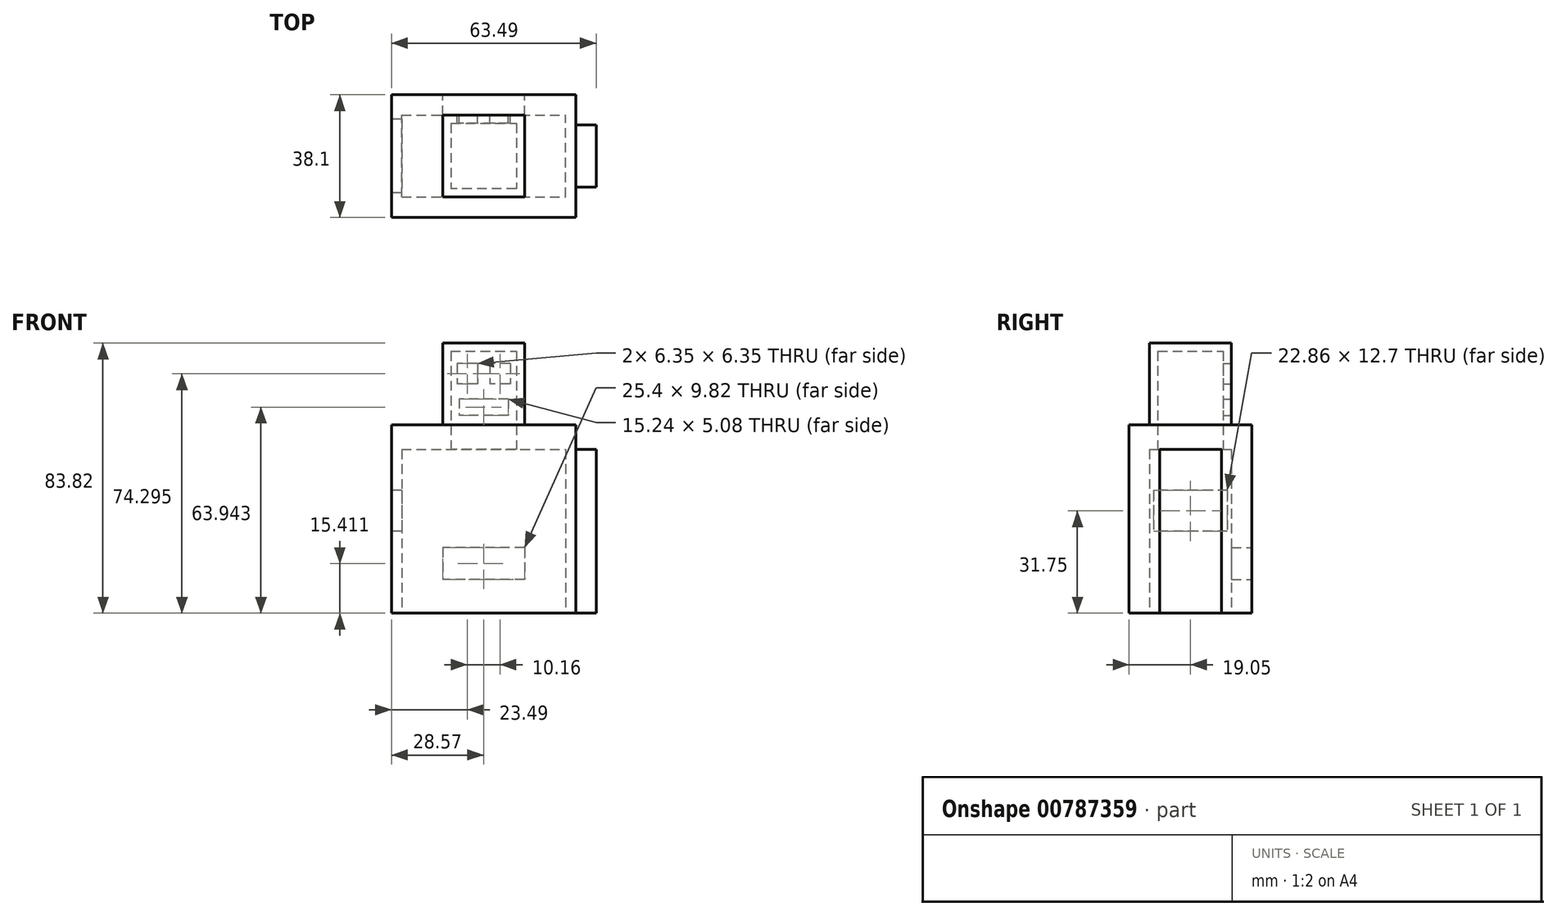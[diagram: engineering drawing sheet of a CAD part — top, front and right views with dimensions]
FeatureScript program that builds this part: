
annotation { "Feature Type Name" : "Feature", "Feature Type Description" : "" }
export const myFeature = defineFeature(function(context is Context, id is Id, definition is map)
    precondition{}
    {
        {
            var Q0;
            Q0=qCreatedBy(makeId("Top.planeOp"),FACE);
            var sketch = newSketch(context, id + "F0", { "sketchPlane" : qUnion([Q0])});
            skLineSegment(sketch, "E0.bottom", {"start": v(-28.58, 19.05) * mm, "end": v(28.58, 19.05) * mm});
            skLineSegment(sketch, "E0.top", {"start": v(-28.58, -19.05) * mm, "end": v(28.58, -19.05) * mm});
            skLineSegment(sketch, "E0.left", {"start": v(-28.58, 19.05) * mm, "end": v(-28.58, -19.05) * mm});
            skLineSegment(sketch, "E0.right", {"start": v(28.58, 19.05) * mm, "end": v(28.58, -19.05) * mm});
            skPoint(sketch, "E1", {"position": v(0, 19.05) * mm});
            skPoint(sketch, "E2", {"position": v(-28.58, 0) * mm});
            skSolve(sketch);
        }
        {
            var Q0;
            Q0 = qSketchRegion(id + "F0", true);
            extrude(context, id + "F1", {"entities" : qUnion([Q0]), "depth" : 58.42 * mm, "offsetDistance" : 25.4 * mm});
        }
        {
            var Q0;
            Q0=makeQuery(id+"F1.opExtrude","CAP_FACE",FACE,{"disambiguationData":[OSD([sQuery(id+"F0.wireOp",EDGE,"E0.bottom"),sQuery(id+"F0.wireOp",EDGE,"E0.top"),sQuery(id+"F0.wireOp",EDGE,"E0.left"),sQuery(id+"F0.wireOp",EDGE,"E0.right")])],"isStart":false});
            var sketch = newSketch(context, id + "F2", { "sketchPlane" : qUnion([Q0])});
            skLineSegment(sketch, "E3.bottom", {"start": v(-12.7, 12.7) * mm, "end": v(12.7, 12.7) * mm});
            skLineSegment(sketch, "E3.top", {"start": v(-12.7, -12.7) * mm, "end": v(12.7, -12.7) * mm});
            skLineSegment(sketch, "E3.left", {"start": v(-12.7, 12.7) * mm, "end": v(-12.7, -12.7) * mm});
            skLineSegment(sketch, "E3.right", {"start": v(12.7, 12.7) * mm, "end": v(12.7, -12.7) * mm});
            skPoint(sketch, "E4", {"position": v(0, 12.7) * mm});
            skPoint(sketch, "E5", {"position": v(-12.7, 0) * mm});
            skSolve(sketch);
        }
        {
            var Q0;
            Q0=makeQuery(id+"F2.imprint","IMPRINT",FACE,{"disambiguationData":[TD([[makeQuery(id+"F2.imprint","IMPRINT",EDGE,{"derivedFrom":sQuery(id+"F2.wireOp",EDGE,"E3.bottom")}),-1.0]])]});
            extrude(context, id + "F3", {"entities" : qUnion([Q0]), "operationType" : NewBodyOperationType.ADD, "depth" : 25.4 * mm, "offsetDistance" : 25.4 * mm});
        }
        {
            var Q0;
            Q0=makeQuery(id+"F0.imprint","IMPRINT",FACE,{"disambiguationData":[TD([[makeQuery(id+"F0.imprint","IMPRINT",EDGE,{"derivedFrom":sQuery(id+"F0.wireOp",EDGE,"E0.bottom")}),-1.0]])]});
            var sketch = newSketch(context, id + "F4", { "sketchPlane" : qUnion([Q0])});
            skLineSegment(sketch, "E6.bottom", {"start": v(-25.4, -12.7) * mm, "end": v(25.4, -12.7) * mm});
            skLineSegment(sketch, "E6.top", {"start": v(-25.4, 12.7) * mm, "end": v(25.4, 12.7) * mm});
            skLineSegment(sketch, "E6.left", {"start": v(-25.4, -12.7) * mm, "end": v(-25.4, 12.7) * mm});
            skLineSegment(sketch, "E6.right", {"start": v(25.4, -12.7) * mm, "end": v(25.4, 12.7) * mm});
            skPoint(sketch, "E7", {"position": v(0, -12.7) * mm});
            skPoint(sketch, "E8", {"position": v(-25.4, 0) * mm});
            skSolve(sketch);
        }
        {
            var Q0;
            Q0 = qSketchRegion(id + "F4", true);
            extrude(context, id + "F5", {"entities" : qUnion([Q0]), "operationType" : NewBodyOperationType.REMOVE, "depth" : 50.8 * mm, "offsetDistance" : 25.4 * mm});
        }
        {
            var Q0;
            Q0=makeQuery(id+"F0.imprint","IMPRINT",FACE,{"disambiguationData":[TD([[makeQuery(id+"F0.imprint","IMPRINT",EDGE,{"derivedFrom":sQuery(id+"F0.wireOp",EDGE,"E0.bottom")}),-1.0]])]});
            var sketch = newSketch(context, id + "F6", { "sketchPlane" : qUnion([Q0])});
            skLineSegment(sketch, "E9.bottom", {"start": v(-10.16, -10.16) * mm, "end": v(10.16, -10.16) * mm});
            skLineSegment(sketch, "E9.top", {"start": v(-10.16, 10.16) * mm, "end": v(10.16, 10.16) * mm});
            skLineSegment(sketch, "E9.left", {"start": v(-10.16, -10.16) * mm, "end": v(-10.16, 10.16) * mm});
            skLineSegment(sketch, "E9.right", {"start": v(10.16, -10.16) * mm, "end": v(10.16, 10.16) * mm});
            skPoint(sketch, "E10", {"position": v(0, -10.16) * mm});
            skPoint(sketch, "E11", {"position": v(-10.16, 0) * mm});
            skSolve(sketch);
        }
        {
            var Q0;
            Q0 = qSketchRegion(id + "F6", true);
            extrude(context, id + "F7", {"entities" : qUnion([Q0]), "operationType" : NewBodyOperationType.REMOVE, "depth" : 81.28 * mm, "offsetDistance" : 25.4 * mm});
        }
        {
            var Q0;
            Q0=makeQuery(id+"F1.opExtrude","SWEPT_FACE",FACE,{"disambiguationData":[OSD([sQuery(id+"F0.wireOp",EDGE,"E0.left")])]});
            var sketch = newSketch(context, id + "F8", { "sketchPlane" : qUnion([Q0])});
            skLineSegment(sketch, "E12.bottom", {"start": v(-11.43, 38.1) * mm, "end": v(11.43, 38.1) * mm});
            skLineSegment(sketch, "E12.top", {"start": v(-11.43, 25.4) * mm, "end": v(11.43, 25.4) * mm});
            skLineSegment(sketch, "E12.left", {"start": v(-11.43, 38.1) * mm, "end": v(-11.43, 25.4) * mm});
            skLineSegment(sketch, "E12.right", {"start": v(11.43, 38.1) * mm, "end": v(11.43, 25.4) * mm});
            skPoint(sketch, "E13", {"position": v(0, 38.1) * mm});
            skPoint(sketch, "E14", {"position": v(-11.43, 31.75) * mm});
            skSolve(sketch);
        }
        {
            var Q0;
            Q0 = qSketchRegion(id + "F8", true);
            extrude(context, id + "F9", {"entities" : qUnion([Q0]), "operationType" : NewBodyOperationType.REMOVE, "oppositeDirection" : true, "depth" : 25.4 * mm, "offsetDistance" : 25.4 * mm});
        }
        {
            var Q0;
            Q0=makeQuery(id+"F3.opExtrude","SWEPT_FACE",FACE,{"disambiguationData":[OSD([sQuery(id+"F2.wireOp",EDGE,"E3.bottom")])]});
            var sketch = newSketch(context, id + "F10", { "sketchPlane" : qUnion([Q0])});
            skLineSegment(sketch, "E15.bottom", {"start": v(-8.26, 77.47) * mm, "end": v(-1.9, 77.47) * mm});
            skLineSegment(sketch, "E15.top", {"start": v(-8.26, 71.12) * mm, "end": v(-1.9, 71.12) * mm});
            skLineSegment(sketch, "E15.left", {"start": v(-8.26, 77.47) * mm, "end": v(-8.26, 71.12) * mm});
            skLineSegment(sketch, "E15.right", {"start": v(-1.9, 77.47) * mm, "end": v(-1.9, 71.12) * mm});
            skPoint(sketch, "E16.oppositeSnap0", {"position": v(12.7, 71.12) * mm});
            skLineSegment(sketch, "E16.bottom", {"start": v(1.9, 77.47) * mm, "end": v(8.26, 77.47) * mm});
            skLineSegment(sketch, "E16.top", {"start": v(1.9, 71.12) * mm, "end": v(8.26, 71.12) * mm});
            skLineSegment(sketch, "E16.left", {"start": v(1.9, 77.47) * mm, "end": v(1.9, 71.12) * mm});
            skLineSegment(sketch, "E16.right", {"start": v(8.26, 77.47) * mm, "end": v(8.26, 71.12) * mm});
            skLineSegment(sketch, "E17.bottom", {"start": v(-7.62, 66.48) * mm, "end": v(7.62, 66.48) * mm});
            skLineSegment(sketch, "E17.top", {"start": v(-7.62, 61.4) * mm, "end": v(7.62, 61.4) * mm});
            skLineSegment(sketch, "E17.left", {"start": v(-7.62, 66.48) * mm, "end": v(-7.62, 61.4) * mm});
            skLineSegment(sketch, "E17.right", {"start": v(7.62, 66.48) * mm, "end": v(7.62, 61.4) * mm});
            skPoint(sketch, "E18", {"position": v(-5.08, 71.12) * mm});
            skPoint(sketch, "E19", {"position": v(5.08, 71.12) * mm});
            skPoint(sketch, "E20", {"position": v(0, 66.48) * mm});
            skSolve(sketch);
        }
        {
            var Q0;
            Q0 = qSketchRegion(id + "F10", true);
            extrude(context, id + "F11", {"entities" : qUnion([Q0]), "operationType" : NewBodyOperationType.REMOVE, "oppositeDirection" : true, "depth" : 12.7 * mm, "offsetDistance" : 25.4 * mm});
        }
        {
            var Q0;
            Q0=makeQuery(id+"F1.opExtrude","SWEPT_FACE",FACE,{"disambiguationData":[OSD([sQuery(id+"F0.wireOp",EDGE,"E0.bottom")])]});
            var sketch = newSketch(context, id + "F12", { "sketchPlane" : qUnion([Q0])});
            skLineSegment(sketch, "E21.bottom", {"start": v(-12.7, 20.32) * mm, "end": v(12.7, 20.32) * mm});
            skLineSegment(sketch, "E21.top", {"start": v(-12.7, 10.5) * mm, "end": v(12.7, 10.5) * mm});
            skLineSegment(sketch, "E21.left", {"start": v(-12.7, 20.32) * mm, "end": v(-12.7, 10.5) * mm});
            skLineSegment(sketch, "E21.right", {"start": v(12.7, 20.32) * mm, "end": v(12.7, 10.5) * mm});
            skPoint(sketch, "E22", {"position": v(0, 20.32) * mm});
            skSolve(sketch);
        }
        {
            var Q0;
            Q0 = qSketchRegion(id + "F12", true);
            extrude(context, id + "F13", {"entities" : qUnion([Q0]), "operationType" : NewBodyOperationType.REMOVE, "oppositeDirection" : true, "depth" : 12.7 * mm, "offsetDistance" : 25.4 * mm});
        }
        {
            var Q0;
            Q0=makeQuery(id+"F1.opExtrude","SWEPT_FACE",FACE,{"disambiguationData":[OSD([sQuery(id+"F0.wireOp",EDGE,"E0.right")])]});
            var sketch = newSketch(context, id + "F14", { "sketchPlane" : qUnion([Q0])});
            skLineSegment(sketch, "E23.bottom", {"start": v(-9.6, 0) * mm, "end": v(9.6, 0) * mm});
            skLineSegment(sketch, "E23.top", {"start": v(-9.6, 50.8) * mm, "end": v(9.6, 50.8) * mm});
            skLineSegment(sketch, "E23.left", {"start": v(-9.6, 0) * mm, "end": v(-9.6, 50.8) * mm});
            skLineSegment(sketch, "E23.right", {"start": v(9.6, 0) * mm, "end": v(9.6, 50.8) * mm});
            skPoint(sketch, "E24", {"position": v(0, 50.8) * mm});
            skSolve(sketch);
        }
        {
            var Q0;
            Q0 = qSketchRegion(id + "F14", true);
            extrude(context, id + "F15", {"entities" : qUnion([Q0]), "operationType" : NewBodyOperationType.ADD, "depth" : 6.35 * mm, "offsetDistance" : 25.4 * mm});
        }
    });
